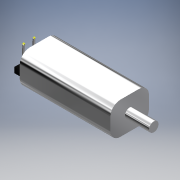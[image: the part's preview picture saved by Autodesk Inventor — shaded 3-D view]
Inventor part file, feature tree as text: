
AUTODESK INVENTOR PART (.ipt)
format: ipt  version: 2018 (Build 220112000, 112)  size: 217,088 bytes
history: native  units: in
note: dims shown in document units (in); Inventor stores cm internally (conversion verified against a paired STEP export)
features: sketch x5, extrude x3, fillet x1, sweep x1, plane x1, chamfer x1
ambient origin geometry x8: Origin, YZ Plane, XZ Plane, XY Plane, X Axis, Y Axis, Z Axis, Center Point
bodies: Solid1 (feature_tree)
feature tree (12):
  extrude  "Extrusion1"  Depth=0.48in
  fillet  "Fillet1"  Radius=1.125in
  extrude  "Extrusion2"  Depth=0.118in
  sweep  "Sweep1"
  plane  "Work Plane1"
  extrude  "Extrusion3"  TaperAngle=0.0deg  [1 undecoded]
  chamfer  "Chamfer1"  Distance=0.07in
  sketch  "Sketch1"  dims[d0=0.4in d1=0.48in d2=1.125in d3=0.0in]
  sketch  "Sketch2"  dims[d4=0.125in d5=0.118in]
  sketch  "Sketch3"  dims[d6=0.3in d7=0.0in d8=0.02in]
  sketch  "Sketch4"  dims[d9=0.015in d10=0.0in d11=0.0in]
  sketch  "Sketch5"  dims[d12=0.125in d13=0.07in d14=0.0in d15=0.006in d16=0.125in d17=45.0deg]
note: 1 required parameter value undecoded (feature->parameter linkage not recoverable at this tier; creation-order binding heuristic only, values carry confidence <= 0.55)
